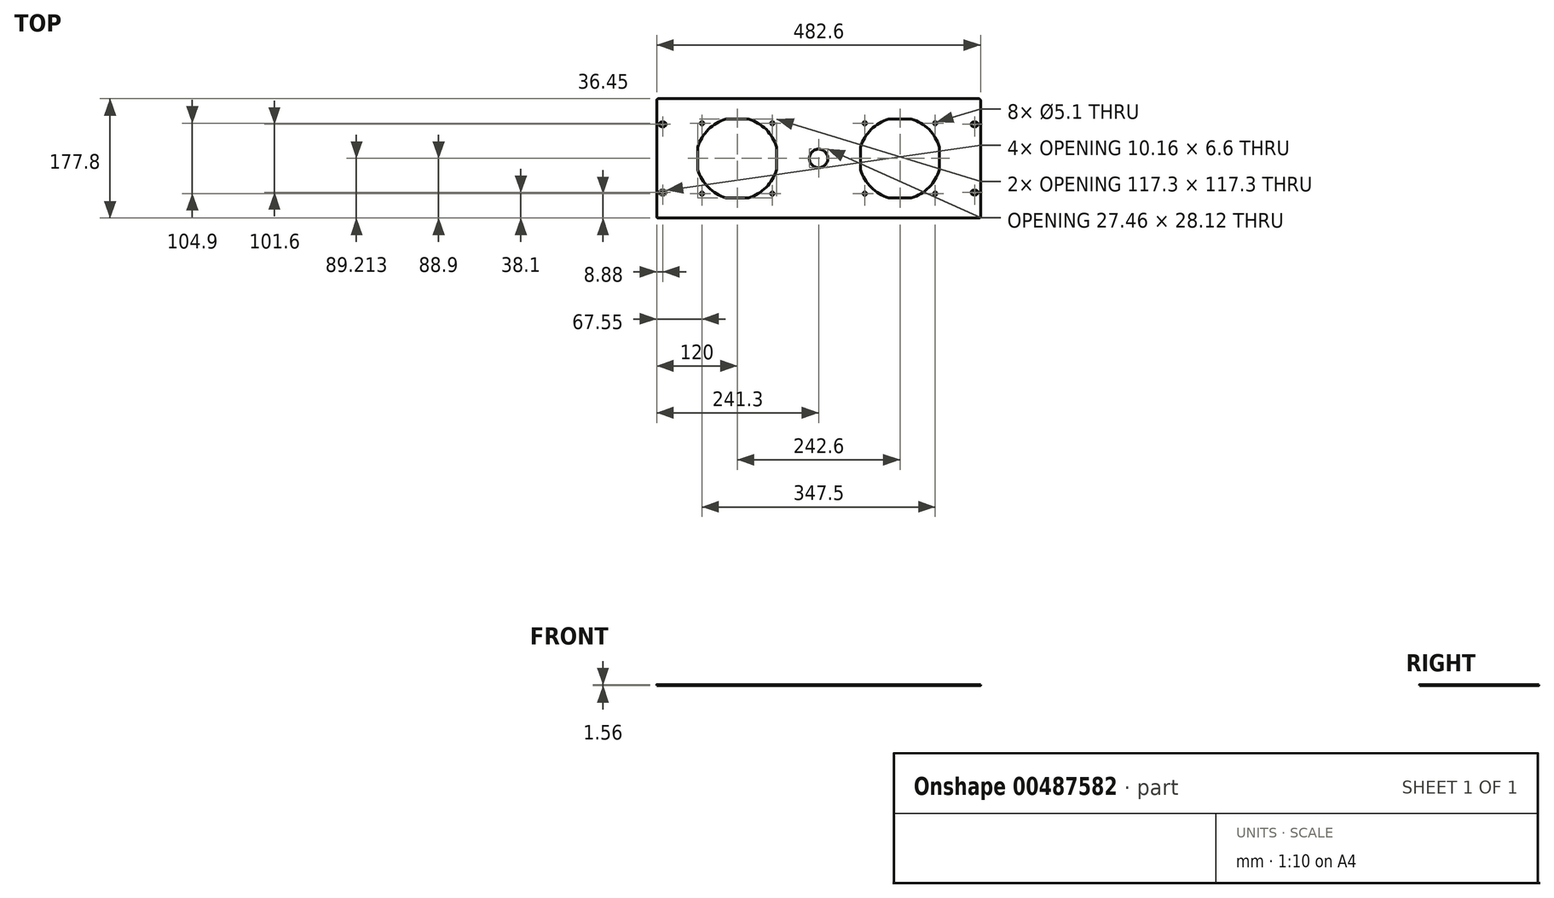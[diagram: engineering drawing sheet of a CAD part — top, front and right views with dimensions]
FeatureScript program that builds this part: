
annotation { "Feature Type Name" : "Feature", "Feature Type Description" : "" }
export const myFeature = defineFeature(function(context is Context, id is Id, definition is map)
    precondition{}
    {
        {
            var Q0;
            Q0=qCreatedBy(makeId("Top.planeOp"),FACE);
            var sketch = newSketch(context, id + "F0", { "sketchPlane" : qUnion([Q0])});
            skLineSegment(sketch, "E0.bottom", {"start": v(0, 0) * mm, "end": v(482.6, 0) * mm});
            skLineSegment(sketch, "E0.top", {"start": v(0, 177.8) * mm, "end": v(482.6, 177.8) * mm});
            skLineSegment(sketch, "E0.left", {"start": v(0, 0) * mm, "end": v(0, 177.8) * mm});
            skLineSegment(sketch, "E0.right", {"start": v(482.6, 0) * mm, "end": v(482.6, 177.8) * mm});
            skLineSegment(sketch, "E1", {"start": v(8.88, 0) * mm, "end": v(8.88, 38.1) * mm, "construction": true});
            skLineSegment(sketch, "E2", {"start": v(8.88, 177.8) * mm, "end": v(8.88, 139.7) * mm, "construction": true});
            skLineSegment(sketch, "E3.bottom", {"start": v(10.76, 41.4) * mm, "end": v(7, 41.4) * mm});
            skLineSegment(sketch, "E3.top", {"start": v(10.76, 34.8) * mm, "end": v(7, 34.8) * mm});
            skLineSegment(sketch, "E3.left", {"start": v(13.96, 38.2) * mm, "end": v(13.96, 38) * mm});
            skLineSegment(sketch, "E3.right", {"start": v(3.8, 38.2) * mm, "end": v(3.8, 38) * mm});
            skPoint(sketch, "E3.middle", {"position": v(8.88, 38.1) * mm});
            skLineSegment(sketch, "E4.bottom", {"start": v(7, 136.4) * mm, "end": v(10.76, 136.4) * mm});
            skLineSegment(sketch, "E4.top", {"start": v(7, 143) * mm, "end": v(10.76, 143) * mm});
            skLineSegment(sketch, "E4.left", {"start": v(3.8, 139.6) * mm, "end": v(3.8, 139.8) * mm});
            skLineSegment(sketch, "E4.right", {"start": v(13.96, 139.6) * mm, "end": v(13.96, 139.8) * mm});
            skPoint(sketch, "E4.middle", {"position": v(8.88, 139.7) * mm});
            skPoint(sketch, "E5.visualSharp", {"position": v(3.8, 143) * mm});
            skArc(sketch, "E5.filletArc", {"start": v(7, 143) * mm, "mid": v(4.74, 142.06) * mm, "end": v(3.8, 139.8) * mm});
            skPoint(sketch, "E6.visualSharp", {"position": v(3.8, 136.4) * mm});
            skArc(sketch, "E6.filletArc", {"start": v(3.8, 139.6) * mm, "mid": v(4.74, 137.34) * mm, "end": v(7, 136.4) * mm});
            skPoint(sketch, "E7.visualSharp", {"position": v(13.96, 143) * mm});
            skArc(sketch, "E7.filletArc", {"start": v(13.96, 139.8) * mm, "mid": v(13.02, 142.06) * mm, "end": v(10.76, 143) * mm});
            skPoint(sketch, "E8.visualSharp", {"position": v(13.96, 136.4) * mm});
            skArc(sketch, "E8.filletArc", {"start": v(10.76, 136.4) * mm, "mid": v(13.02, 137.34) * mm, "end": v(13.96, 139.6) * mm});
            skPoint(sketch, "E9.visualSharp", {"position": v(3.8, 41.4) * mm});
            skArc(sketch, "E9.filletArc", {"start": v(7, 41.4) * mm, "mid": v(4.74, 40.46) * mm, "end": v(3.8, 38.2) * mm});
            skPoint(sketch, "E10.visualSharp", {"position": v(3.8, 34.8) * mm});
            skArc(sketch, "E10.filletArc", {"start": v(3.8, 38) * mm, "mid": v(4.74, 35.74) * mm, "end": v(7, 34.8) * mm});
            skPoint(sketch, "E11.visualSharp", {"position": v(13.96, 41.4) * mm});
            skArc(sketch, "E11.filletArc", {"start": v(13.96, 38.2) * mm, "mid": v(13.02, 40.46) * mm, "end": v(10.76, 41.4) * mm});
            skPoint(sketch, "E12.visualSharp", {"position": v(13.96, 34.8) * mm});
            skArc(sketch, "E12.filletArc", {"start": v(10.76, 34.8) * mm, "mid": v(13.02, 35.74) * mm, "end": v(13.96, 38) * mm});
            skLineSegment(sketch, "E13", {"start": v(241.3, 0) * mm, "end": v(241.3, 101.4) * mm, "construction": true});
            skLineSegment(sketch, "E14.MirrorCS", {"start": v(478.8, 139.6) * mm, "end": v(478.8, 139.8) * mm});
            skLineSegment(sketch, "E15.MirrorCS", {"start": v(468.64, 139.6) * mm, "end": v(468.64, 139.8) * mm});
            skArc(sketch, "E16.MirrorCS", {"start": v(471.84, 136.4) * mm, "mid": v(469.58, 137.34) * mm, "end": v(468.64, 139.6) * mm});
            skArc(sketch, "E17.MirrorCS", {"start": v(475.6, 143) * mm, "mid": v(477.86, 142.06) * mm, "end": v(478.8, 139.8) * mm});
            skArc(sketch, "E18.MirrorCS", {"start": v(478.8, 139.6) * mm, "mid": v(477.86, 137.34) * mm, "end": v(475.6, 136.4) * mm});
            skPoint(sketch, "E19.MirrorP", {"position": v(473.72, 139.7) * mm});
            skArc(sketch, "E20.MirrorCS", {"start": v(468.64, 139.8) * mm, "mid": v(469.58, 142.06) * mm, "end": v(471.84, 143) * mm});
            skLineSegment(sketch, "E21.MirrorCS", {"start": v(475.6, 143) * mm, "end": v(471.84, 143) * mm});
            skLineSegment(sketch, "E22.MirrorCS", {"start": v(475.6, 136.4) * mm, "end": v(471.84, 136.4) * mm});
            skLineSegment(sketch, "E23.MirrorCS", {"start": v(473.72, 177.8) * mm, "end": v(473.72, 139.7) * mm, "construction": true});
            skPoint(sketch, "E24.MirrorP", {"position": v(478.8, 143) * mm});
            skPoint(sketch, "E25.MirrorP", {"position": v(478.8, 136.4) * mm});
            skPoint(sketch, "E26.MirrorP", {"position": v(468.64, 143) * mm});
            skPoint(sketch, "E27.MirrorP", {"position": v(468.64, 136.4) * mm});
            skLineSegment(sketch, "E28.MirrorCS", {"start": v(468.64, 38.2) * mm, "end": v(468.64, 38) * mm});
            skLineSegment(sketch, "E29.MirrorCS", {"start": v(478.8, 38.2) * mm, "end": v(478.8, 38) * mm});
            skArc(sketch, "E30.MirrorCS", {"start": v(475.6, 41.4) * mm, "mid": v(477.86, 40.46) * mm, "end": v(478.8, 38.2) * mm});
            skArc(sketch, "E31.MirrorCS", {"start": v(471.84, 34.8) * mm, "mid": v(469.58, 35.74) * mm, "end": v(468.64, 38) * mm});
            skLineSegment(sketch, "E32.MirrorCS", {"start": v(471.84, 41.4) * mm, "end": v(475.6, 41.4) * mm});
            skLineSegment(sketch, "E33.MirrorCS", {"start": v(471.84, 34.8) * mm, "end": v(475.6, 34.8) * mm});
            skArc(sketch, "E34.MirrorCS", {"start": v(478.8, 38) * mm, "mid": v(477.86, 35.74) * mm, "end": v(475.6, 34.8) * mm});
            skArc(sketch, "E35.MirrorCS", {"start": v(468.64, 38.2) * mm, "mid": v(469.58, 40.46) * mm, "end": v(471.84, 41.4) * mm});
            skPoint(sketch, "E36.MirrorP", {"position": v(478.8, 34.8) * mm});
            skLineSegment(sketch, "E37.MirrorCS", {"start": v(473.72, 0) * mm, "end": v(473.72, 38.1) * mm, "construction": true});
            skPoint(sketch, "E38.MirrorP", {"position": v(473.72, 38.1) * mm});
            skPoint(sketch, "E39.MirrorP", {"position": v(468.64, 34.8) * mm});
            skPoint(sketch, "E40.MirrorP", {"position": v(468.64, 41.4) * mm});
            skPoint(sketch, "E41.MirrorP", {"position": v(478.8, 41.4) * mm});
            skSolve(sketch);
        }
        {
            var Q0;
            Q0 = qSketchRegion(id + "F0", true);
            extrude(context, id + "F1", {"entities" : qUnion([Q0]), "depth" : 1.56 * mm});
        }
        {
            var Q0;
            Q0=makeQuery(id+"F1.opExtrude","SWEPT_EDGE",EDGE,{"disambiguationData":[OSD([sQuery(id+"F0.wireOp",EDGE,"E0.top"),sQuery(id+"F0.wireOp",EDGE,"E0.left")])]});
            var Q1;
            Q1=makeQuery(id+"F1.opExtrude","SWEPT_EDGE",EDGE,{"disambiguationData":[OSD([sQuery(id+"F0.wireOp",EDGE,"E0.bottom"),sQuery(id+"F0.wireOp",EDGE,"E0.left")])]});
            var Q2;
            Q2=makeQuery(id+"F1.opExtrude","SWEPT_EDGE",EDGE,{"disambiguationData":[OSD([sQuery(id+"F0.wireOp",EDGE,"E0.top"),sQuery(id+"F0.wireOp",EDGE,"E0.right")])]});
            var Q3;
            Q3=makeQuery(id+"F1.opExtrude","SWEPT_EDGE",EDGE,{"disambiguationData":[OSD([sQuery(id+"F0.wireOp",EDGE,"E0.bottom"),sQuery(id+"F0.wireOp",EDGE,"E0.right")])]});
            fillet(context, id + "F2", {"entities" : qUnion([Q0, Q1, Q2, Q3]), "radius" : 2.5 * mm, "tangentPropagation" : true, "allowEdgeOverflow" : false});
        }
        {
            var Q0;
            Q0=makeQuery(id+"F1.opExtrude","CAP_FACE",FACE,{"disambiguationData":[OSD([sQuery(id+"F0.wireOp",EDGE,"E0.bottom"),sQuery(id+"F0.wireOp",EDGE,"E0.top"),sQuery(id+"F0.wireOp",EDGE,"E0.left"),sQuery(id+"F0.wireOp",EDGE,"E0.right"),sQuery(id+"F0.wireOp",EDGE,"E3.bottom"),sQuery(id+"F0.wireOp",EDGE,"E3.top"),sQuery(id+"F0.wireOp",EDGE,"E3.left"),sQuery(id+"F0.wireOp",EDGE,"E3.right"),sQuery(id+"F0.wireOp",EDGE,"E4.bottom"),sQuery(id+"F0.wireOp",EDGE,"E4.top"),sQuery(id+"F0.wireOp",EDGE,"E4.left"),sQuery(id+"F0.wireOp",EDGE,"E4.right"),sQuery(id+"F0.wireOp",EDGE,"E5.filletArc"),sQuery(id+"F0.wireOp",EDGE,"E6.filletArc"),sQuery(id+"F0.wireOp",EDGE,"E7.filletArc"),sQuery(id+"F0.wireOp",EDGE,"E8.filletArc"),sQuery(id+"F0.wireOp",EDGE,"E9.filletArc"),sQuery(id+"F0.wireOp",EDGE,"E10.filletArc"),sQuery(id+"F0.wireOp",EDGE,"E11.filletArc"),sQuery(id+"F0.wireOp",EDGE,"E12.filletArc"),sQuery(id+"F0.wireOp",EDGE,"E14.MirrorCS"),sQuery(id+"F0.wireOp",EDGE,"E15.MirrorCS"),sQuery(id+"F0.wireOp",EDGE,"E16.MirrorCS"),sQuery(id+"F0.wireOp",EDGE,"E17.MirrorCS"),sQuery(id+"F0.wireOp",EDGE,"E18.MirrorCS"),sQuery(id+"F0.wireOp",EDGE,"E20.MirrorCS"),sQuery(id+"F0.wireOp",EDGE,"E21.MirrorCS"),sQuery(id+"F0.wireOp",EDGE,"E22.MirrorCS"),sQuery(id+"F0.wireOp",EDGE,"E28.MirrorCS"),sQuery(id+"F0.wireOp",EDGE,"E29.MirrorCS"),sQuery(id+"F0.wireOp",EDGE,"E30.MirrorCS"),sQuery(id+"F0.wireOp",EDGE,"E31.MirrorCS"),sQuery(id+"F0.wireOp",EDGE,"E32.MirrorCS"),sQuery(id+"F0.wireOp",EDGE,"E33.MirrorCS"),sQuery(id+"F0.wireOp",EDGE,"E34.MirrorCS"),sQuery(id+"F0.wireOp",EDGE,"E35.MirrorCS")])],"isStart":false});
            var sketch = newSketch(context, id + "F3", { "sketchPlane" : qUnion([Q0])});
            skArc(sketch, "E42", {"start": v(103.23, 147.55) * mm, "mid": v(76.87, 132.03) * mm, "end": v(61.35, 105.67) * mm});
            skLineSegment(sketch, "E43.bottom", {"start": v(178.65, 147.55) * mm, "end": v(61.35, 147.55) * mm, "construction": true});
            skLineSegment(sketch, "E43.top", {"start": v(178.65, 30.25) * mm, "end": v(61.35, 30.25) * mm, "construction": true});
            skLineSegment(sketch, "E43.left", {"start": v(178.65, 147.55) * mm, "end": v(178.65, 30.25) * mm, "construction": true});
            skLineSegment(sketch, "E43.right", {"start": v(61.35, 147.55) * mm, "end": v(61.35, 30.25) * mm, "construction": true});
            skCircle(sketch, "E44", {"center": v(67.55, 141.35) * mm, "radius": 2.55 * mm});
            skArc(sketch, "E45.trimOffspring", {"start": v(61.35, 72.13) * mm, "mid": v(76.87, 45.77) * mm, "end": v(103.23, 30.25) * mm});
            skArc(sketch, "E46.trimOffspring", {"start": v(178.65, 105.67) * mm, "mid": v(163.13, 132.03) * mm, "end": v(136.77, 147.55) * mm});
            skArc(sketch, "E47.trimOffspring", {"start": v(136.77, 30.25) * mm, "mid": v(163.13, 45.77) * mm, "end": v(178.65, 72.13) * mm});
            skLineSegment(sketch, "E48", {"start": v(61.35, 105.67) * mm, "end": v(61.35, 72.13) * mm});
            skLineSegment(sketch, "E49", {"start": v(103.23, 30.25) * mm, "end": v(136.77, 30.25) * mm});
            skLineSegment(sketch, "E50", {"start": v(178.65, 72.13) * mm, "end": v(178.65, 105.67) * mm});
            skLineSegment(sketch, "E51", {"start": v(136.77, 147.55) * mm, "end": v(103.23, 147.55) * mm});
            skLineSegment(sketch, "E52.0", {"start": v(0, 2.5) * mm, "end": v(0, 175.3) * mm, "construction": true});
            skLineSegment(sketch, "E52.1", {"start": v(2.5, 0) * mm, "end": v(480.1, 0) * mm, "construction": true});
            skCircle(sketch, "E53.0.1.0", {"center": v(67.55, 36.45) * mm, "radius": 2.55 * mm});
            skCircle(sketch, "E53.1.0.0", {"center": v(172.45, 141.35) * mm, "radius": 2.55 * mm});
            skCircle(sketch, "E53.1.1.0", {"center": v(172.45, 36.45) * mm, "radius": 2.55 * mm});
            skLineSegment(sketch, "E53.direction1", {"start": v(67.55, 141.35) * mm, "end": v(172.45, 141.35) * mm, "construction": true});
            skLineSegment(sketch, "E53.direction2", {"start": v(67.55, 141.35) * mm, "end": v(67.55, 36.45) * mm, "construction": true});
            skArc(sketch, "E54.1.0.0", {"start": v(345.83, 147.55) * mm, "mid": v(319.47, 132.03) * mm, "end": v(303.95, 105.67) * mm});
            skLineSegment(sketch, "E54.1.0.1", {"start": v(421.25, 147.55) * mm, "end": v(303.95, 147.55) * mm, "construction": true});
            skLineSegment(sketch, "E54.1.0.2", {"start": v(421.25, 30.25) * mm, "end": v(303.95, 30.25) * mm, "construction": true});
            skLineSegment(sketch, "E54.1.0.3", {"start": v(421.25, 147.55) * mm, "end": v(421.25, 30.25) * mm, "construction": true});
            skLineSegment(sketch, "E54.1.0.4", {"start": v(303.95, 147.55) * mm, "end": v(303.95, 30.25) * mm, "construction": true});
            skPoint(sketch, "E54.1.0.5", {"position": v(362.6, 88.9) * mm});
            skLineSegment(sketch, "E54.1.0.6", {"start": v(310.15, 141.35) * mm, "end": v(415.05, 141.35) * mm, "construction": true});
            skArc(sketch, "E54.1.0.7", {"start": v(303.95, 72.13) * mm, "mid": v(319.47, 45.77) * mm, "end": v(345.83, 30.25) * mm});
            skArc(sketch, "E54.1.0.8", {"start": v(421.25, 105.67) * mm, "mid": v(405.73, 132.03) * mm, "end": v(379.37, 147.55) * mm});
            skArc(sketch, "E54.1.0.9", {"start": v(379.37, 30.25) * mm, "mid": v(405.73, 45.77) * mm, "end": v(421.25, 72.13) * mm});
            skLineSegment(sketch, "E54.1.0.10", {"start": v(310.15, 141.35) * mm, "end": v(310.15, 36.45) * mm, "construction": true});
            skLineSegment(sketch, "E54.1.0.11", {"start": v(421.25, 72.13) * mm, "end": v(421.25, 105.67) * mm});
            skLineSegment(sketch, "E54.1.0.12", {"start": v(379.37, 147.55) * mm, "end": v(345.83, 147.55) * mm});
            skLineSegment(sketch, "E54.1.0.13", {"start": v(345.83, 30.25) * mm, "end": v(379.37, 30.25) * mm});
            skCircle(sketch, "E54.1.0.14", {"center": v(415.05, 36.45) * mm, "radius": 2.55 * mm});
            skLineSegment(sketch, "E54.1.0.15", {"start": v(303.95, 105.67) * mm, "end": v(303.95, 72.13) * mm});
            skCircle(sketch, "E54.1.0.16", {"center": v(310.15, 36.45) * mm, "radius": 2.55 * mm});
            skCircle(sketch, "E54.1.0.17", {"center": v(415.05, 141.35) * mm, "radius": 2.55 * mm});
            skCircle(sketch, "E54.1.0.18", {"center": v(310.15, 141.35) * mm, "radius": 2.55 * mm});
            skLineSegment(sketch, "E54.direction1", {"start": v(61.35, 30.25) * mm, "end": v(303.95, 30.25) * mm, "construction": true});
            skLineSegment(sketch, "E55", {"start": v(120, 88.9) * mm, "end": v(362.6, 88.9) * mm, "construction": true});
            skArc(sketch, "E56", {"start": v(239.8, 102.57) * mm, "mid": v(241.3, 75.15) * mm, "end": v(242.8, 102.57) * mm});
            skLineSegment(sketch, "E57", {"start": v(241.3, 88.9) * mm, "end": v(241.3, 103.28) * mm, "construction": true});
            skLineSegment(sketch, "E58", {"start": v(241.3, 103.28) * mm, "end": v(239.8, 103.28) * mm});
            skLineSegment(sketch, "E59", {"start": v(241.3, 103.28) * mm, "end": v(242.8, 103.28) * mm});
            skLineSegment(sketch, "E60", {"start": v(239.8, 103.28) * mm, "end": v(239.8, 102.57) * mm});
            skLineSegment(sketch, "E61", {"start": v(242.8, 103.28) * mm, "end": v(242.8, 102.57) * mm});
            skSolve(sketch);
        }
        {
            var Q0;
            Q0 = qSketchRegion(id + "F3", true);
            extrude(context, id + "F4", {"entities" : qUnion([Q0]), "operationType" : NewBodyOperationType.REMOVE, "oppositeDirection" : true, "depth" : 25 * mm});
        }
    });
